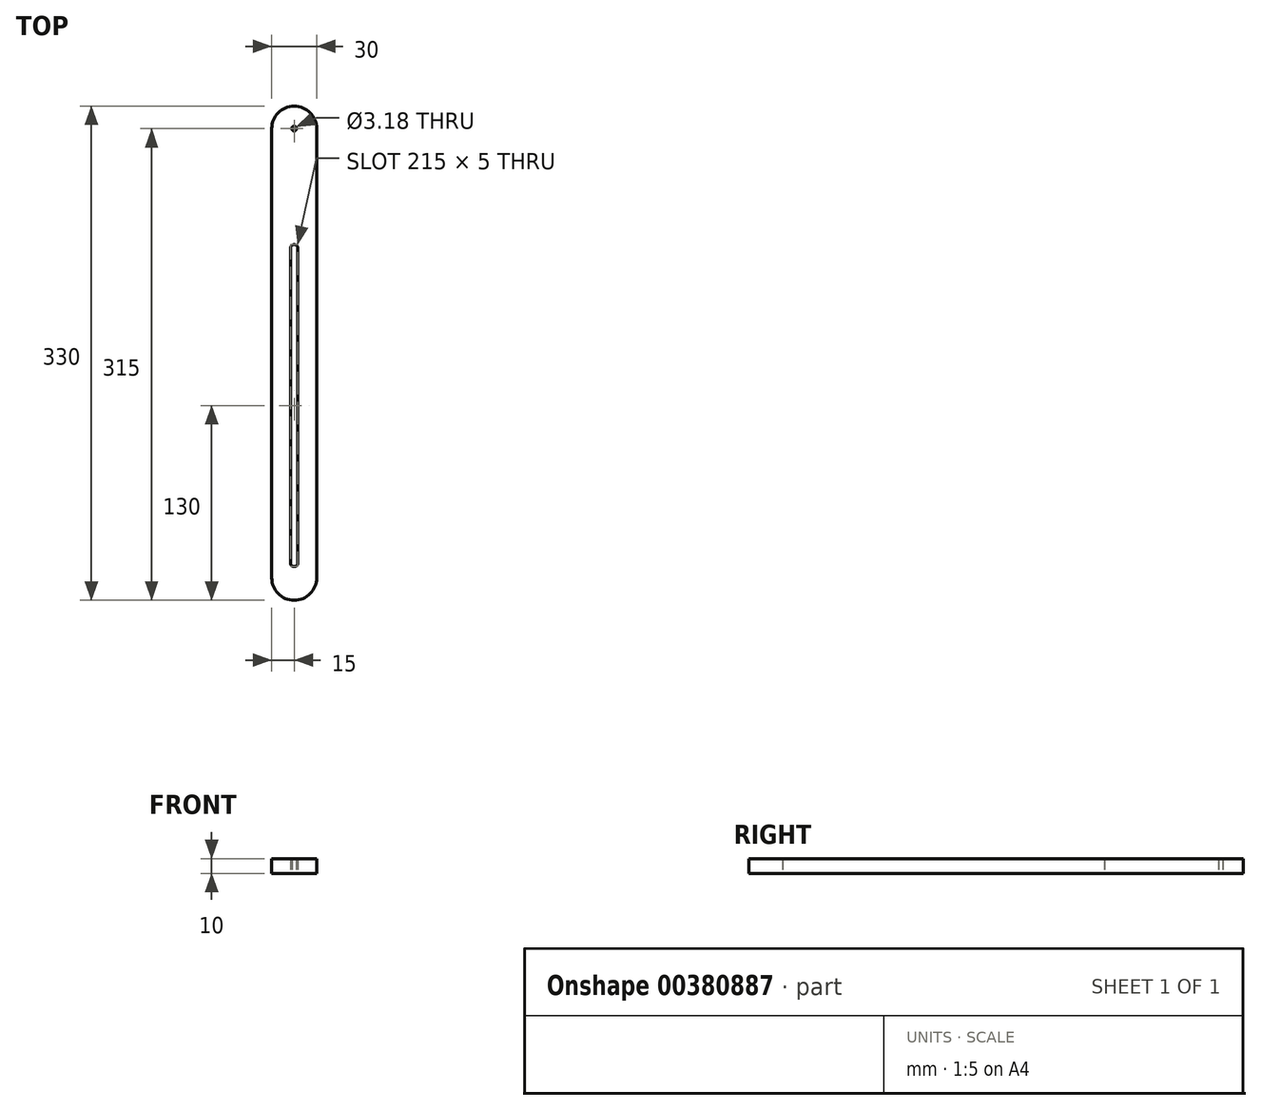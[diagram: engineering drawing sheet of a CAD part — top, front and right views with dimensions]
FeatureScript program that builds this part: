
annotation { "Feature Type Name" : "Feature", "Feature Type Description" : "" }
export const myFeature = defineFeature(function(context is Context, id is Id, definition is map)
    precondition{}
    {
        {
            var Q0;
            Q0=qCreatedBy(makeId("Top.planeOp"),FACE);
            var sketch = newSketch(context, id + "F0", { "sketchPlane" : qUnion([Q0])});
            skLineSegment(sketch, "E0", {"start": v(0, 0) * mm, "end": v(0, -300) * mm});
            skArc(sketch, "E1.0.startCap", {"start": v(-15, 0) * mm, "mid": v(0, 15) * mm, "end": v(15, 0) * mm});
            skArc(sketch, "E1.0.endCap", {"start": v(15, -300) * mm, "mid": v(0, -315) * mm, "end": v(-15, -300) * mm});
            skLineSegment(sketch, "E1.0.left", {"start": v(15, 0) * mm, "end": v(15, -300) * mm});
            skLineSegment(sketch, "E1.0.right", {"start": v(-15, 0) * mm, "end": v(-15, -300) * mm});
            skLineSegment(sketch, "E2", {"start": v(0, -80) * mm, "end": v(0, -290) * mm});
            skArc(sketch, "E3.0.startCap", {"start": v(-2.5, -80) * mm, "mid": v(0, -77.5) * mm, "end": v(2.5, -80) * mm});
            skArc(sketch, "E3.0.endCap", {"start": v(2.5, -290) * mm, "mid": v(0, -292.5) * mm, "end": v(-2.5, -290) * mm});
            skLineSegment(sketch, "E3.0.left", {"start": v(2.5, -80) * mm, "end": v(2.5, -290) * mm});
            skLineSegment(sketch, "E3.0.right", {"start": v(-2.5, -80) * mm, "end": v(-2.5, -290) * mm});
            skCircle(sketch, "E4", {"center": v(0, 0) * mm, "radius": 1.6 * mm});
            skSolve(sketch);
        }
        {
            var Q0;
            Q0 = qSketchRegion(id + "F0", true);
            extrude(context, id + "F1", {"entities" : qUnion([Q0]), "depth" : 10 * mm});
        }
    });
